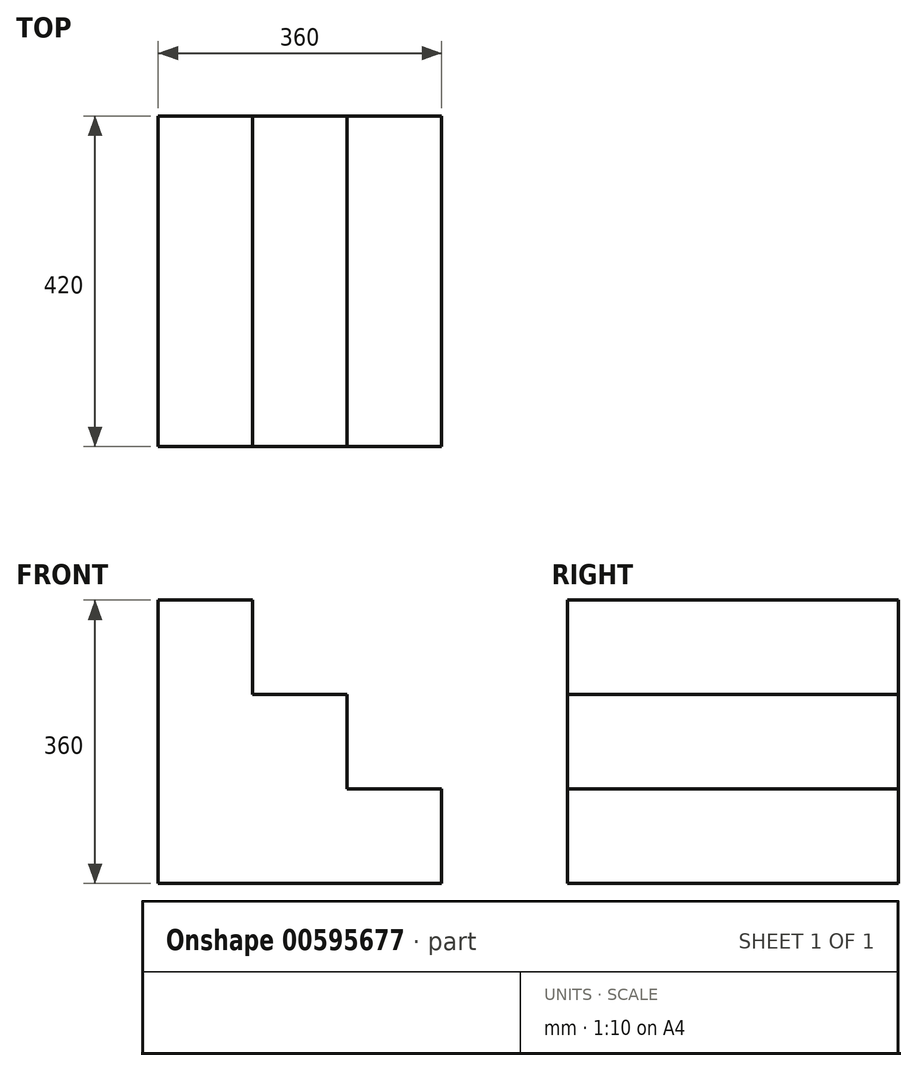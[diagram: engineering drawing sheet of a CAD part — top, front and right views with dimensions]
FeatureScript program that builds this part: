
annotation { "Feature Type Name" : "Feature", "Feature Type Description" : "" }
export const myFeature = defineFeature(function(context is Context, id is Id, definition is map)
    precondition{}
    {
        {
            var Q0;
            Q0=qCreatedBy(makeId("Front.planeOp"),FACE);
            var sketch = newSketch(context, id + "F0", { "sketchPlane" : qUnion([Q0])});
            skLineSegment(sketch, "E0", {"start": v(0, 0) * mm, "end": v(99.85, 0) * mm});
            skLineSegment(sketch, "E1", {"start": v(0, 0) * mm, "end": v(360, 0) * mm});
            skLineSegment(sketch, "E2", {"start": v(360, 0) * mm, "end": v(360, 120) * mm});
            skLineSegment(sketch, "E3", {"start": v(360, 120) * mm, "end": v(240, 120) * mm});
            skLineSegment(sketch, "E4", {"start": v(240, 120) * mm, "end": v(240, 240) * mm});
            skLineSegment(sketch, "E5", {"start": v(240, 240) * mm, "end": v(120, 240) * mm});
            skLineSegment(sketch, "E6", {"start": v(120, 240) * mm, "end": v(120, 360) * mm});
            skLineSegment(sketch, "E7", {"start": v(120, 360) * mm, "end": v(0, 360) * mm});
            skLineSegment(sketch, "E8", {"start": v(0, 360) * mm, "end": v(0, 0) * mm});
            skSolve(sketch);
        }
        {
            var Q0;
            {var subQ0=sQuery(id+"F0.wireOp",EDGE,"E2");Q0=makeQuery(id+"F0.imprint","IMPRINT",FACE,{"disambiguationData":[TD([[makeQuery(id+"F0.imprint","IMPRINT",EDGE,{"derivedFrom":subQ0}),1.0]])]});}
            extrude(context, id + "F1", {"entities" : qUnion([Q0]), "depth" : 420 * mm, "offsetDistance" : 25 * mm});
        }
    });
